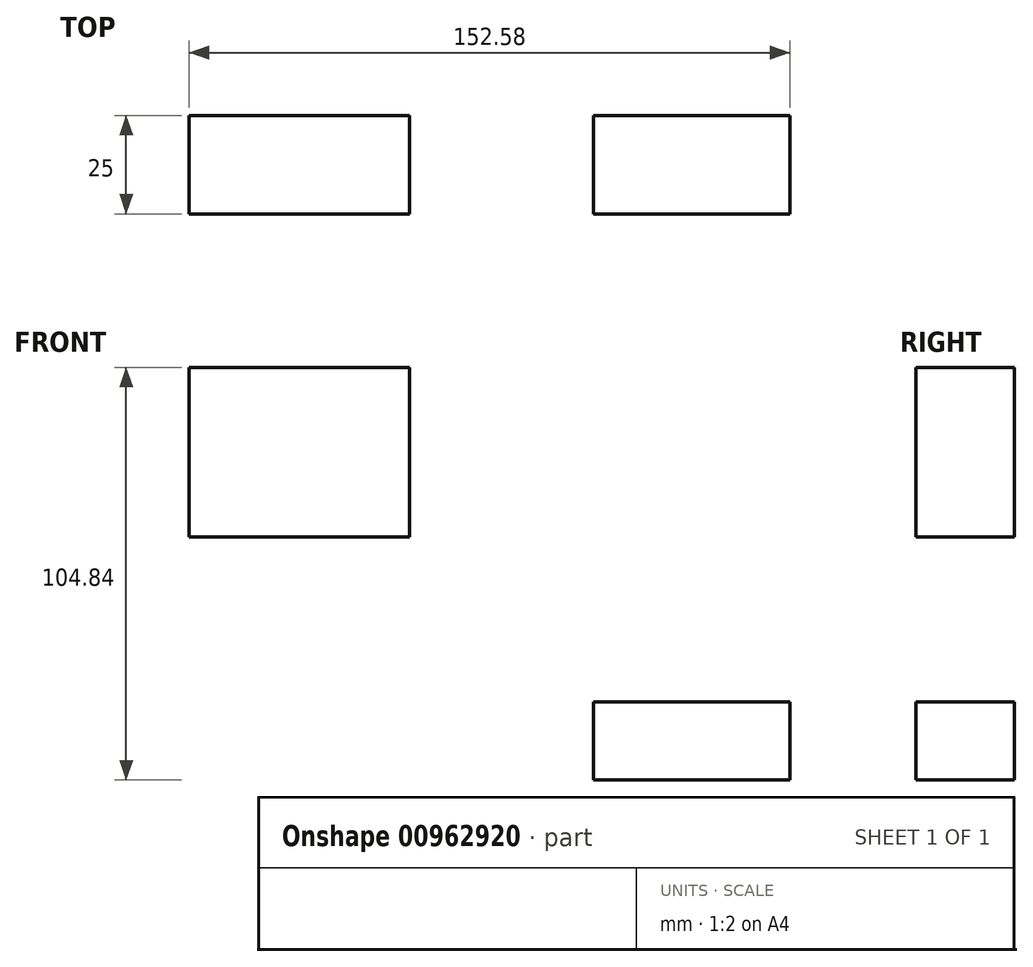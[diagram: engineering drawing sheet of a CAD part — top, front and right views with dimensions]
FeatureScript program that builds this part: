
annotation { "Feature Type Name" : "Feature", "Feature Type Description" : "" }
export const myFeature = defineFeature(function(context is Context, id is Id, definition is map)
    precondition{}
    {
        {
            var Q0;
            Q0=qCreatedBy(makeId("Front.planeOp"),FACE);
            var sketch = newSketch(context, id + "F0", { "sketchPlane" : qUnion([Q0])});
            skLineSegment(sketch, "E0.bottom", {"start": v(-30.35, 113.67) * mm, "end": v(25.63, 113.67) * mm});
            skLineSegment(sketch, "E0.top", {"start": v(-30.35, 70.56) * mm, "end": v(25.63, 70.56) * mm});
            skLineSegment(sketch, "E0.left", {"start": v(-30.35, 113.67) * mm, "end": v(-30.35, 70.56) * mm});
            skLineSegment(sketch, "E0.right", {"start": v(25.63, 113.67) * mm, "end": v(25.63, 70.56) * mm});
            skLineSegment(sketch, "E1.bottom", {"start": v(72.4, 28.7) * mm, "end": v(122.23, 28.7) * mm});
            skLineSegment(sketch, "E1.top", {"start": v(72.4, 8.83) * mm, "end": v(122.23, 8.83) * mm});
            skLineSegment(sketch, "E1.left", {"start": v(72.4, 28.7) * mm, "end": v(72.4, 8.83) * mm});
            skLineSegment(sketch, "E1.right", {"start": v(122.23, 28.7) * mm, "end": v(122.23, 8.83) * mm});
            skSolve(sketch);
        }
        {
            var Q0;
            Q0 = qSketchRegion(id + "F0", true);
            extrude(context, id + "F1", {"entities" : qUnion([Q0]), "depth" : 25 * mm, "offsetDistance" : 25 * mm});
        }
    });
